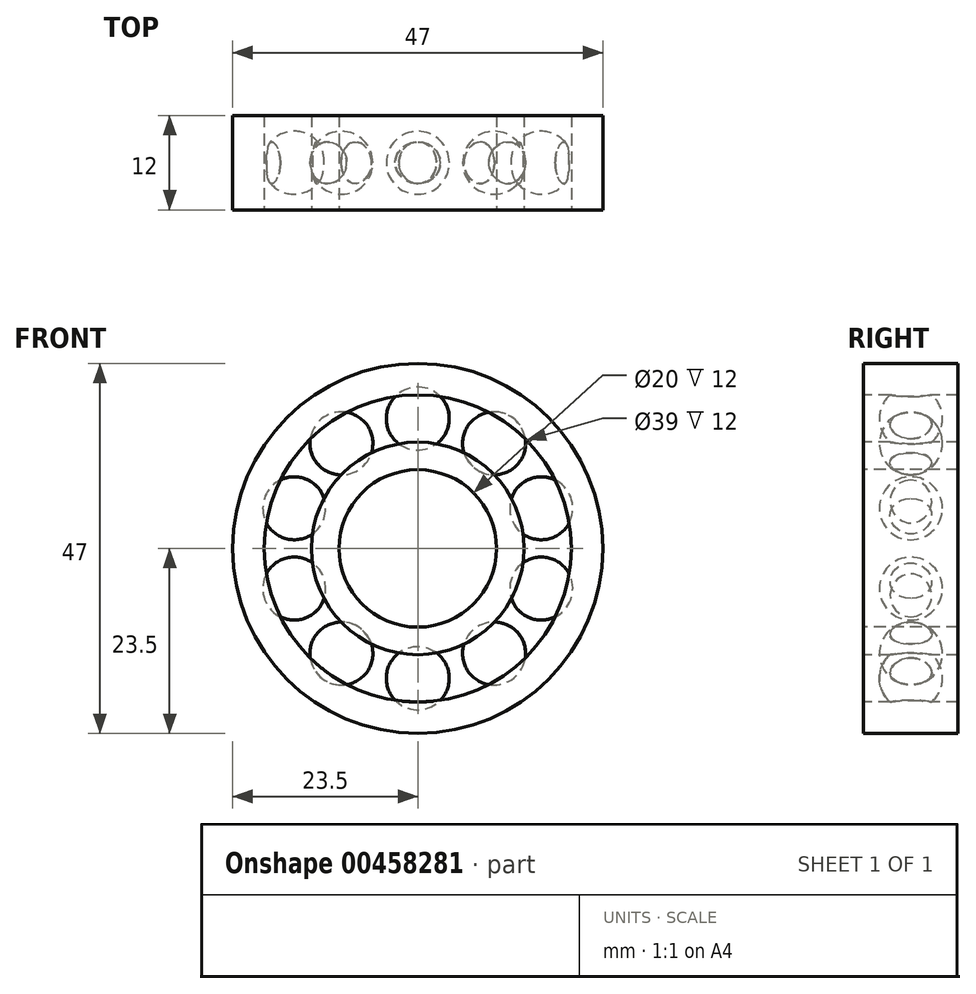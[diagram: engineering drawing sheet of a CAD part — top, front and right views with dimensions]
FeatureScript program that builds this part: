
annotation { "Feature Type Name" : "Feature", "Feature Type Description" : "" }
export const myFeature = defineFeature(function(context is Context, id is Id, definition is map)
    precondition{}
    {
        {
            var Q0;
            Q0=qCreatedBy(makeId("Right.planeOp"),FACE);
            var sketch = newSketch(context, id + "F0", { "sketchPlane" : qUnion([Q0])});
            skLineSegment(sketch, "E0.bottom", {"start": v(-6, 13.5) * mm, "end": v(6, 13.5) * mm});
            skLineSegment(sketch, "E0.top", {"start": v(-6, 10) * mm, "end": v(6, 10) * mm});
            skLineSegment(sketch, "E0.left", {"start": v(-6, 13.5) * mm, "end": v(-6, 10) * mm});
            skLineSegment(sketch, "E0.right", {"start": v(6, 13.5) * mm, "end": v(6, 10) * mm});
            skLineSegment(sketch, "E1.bottom", {"start": v(-6, 23.5) * mm, "end": v(6, 23.5) * mm});
            skLineSegment(sketch, "E1.top", {"start": v(-6, 19.5) * mm, "end": v(6, 19.5) * mm});
            skLineSegment(sketch, "E1.left", {"start": v(-6, 23.5) * mm, "end": v(-6, 19.5) * mm});
            skLineSegment(sketch, "E1.right", {"start": v(6, 23.5) * mm, "end": v(6, 19.5) * mm});
            skLineSegment(sketch, "E2", {"start": v(-39, 0) * mm, "end": v(27.89, 0) * mm, "construction": true});
            skSolve(sketch);
        }
        {
            var Q0;
            Q0 = qSketchRegion(id + "F0", true);
            var Q1;
            Q1=sQuery(id+"F0.wireOp",EDGE,"E2");
            revolve(context, id + "F1", {"entities" : qUnion([Q0]), "axis" : qUnion([Q1]), "revolveType" : RevolveType.FULL});
        }
        {
            var Q0;
            Q0=qCreatedBy(makeId("Front.planeOp"),FACE);
            var sketch = newSketch(context, id + "F2", { "sketchPlane" : qUnion([Q0])});
            skArc(sketch, "E3", {"start": v(0, 12.5) * mm, "mid": v(4, 16.5) * mm, "end": v(0, 20.5) * mm});
            skLineSegment(sketch, "E4", {"start": v(0, 10.56) * mm, "end": v(0, 20.96) * mm, "construction": true});
            skLineSegment(sketch, "E5", {"start": v(0, 20.5) * mm, "end": v(0, 12.5) * mm});
            skPoint(sketch, "E6.center", {"position": v(0, 0) * mm});
            skLineSegment(sketch, "E7", {"start": v(0, 32.3) * mm, "end": v(0, -27.67) * mm, "construction": true});
            skSolve(sketch);
        }
        {
            var Q0;
            Q0 = qSketchRegion(id + "F2", true);
            var Q1;
            Q1=sQuery(id+"F2.wireOp",EDGE,"E4");
            revolve(context, id + "F3", {"entities" : qUnion([Q0]), "axis" : qUnion([Q1]), "revolveType" : RevolveType.FULL});
        }
        {
            var Q0;
            Q0=makeQuery(id+"F3.opRevolve","SWEPT_BODY",BODY,{"disambiguationData":[OSD([sQuery(id+"F2.wireOp",EDGE,"E3"),sQuery(id+"F2.wireOp",EDGE,"E5")])]});
            var Q1;
            Q1=makeQuery(id+"F1.opRevolve","SWEPT_EDGE",EDGE,{"disambiguationData":[OSD([sQuery(id+"F0.wireOp",EDGE,"E0.top"),sQuery(id+"F0.wireOp",EDGE,"E0.left")])]});
            circularPattern(context, id + "F4", {"operationType" : NewBodyOperationType.ADD, "entities" : qUnion([Q0]), "axis" : qUnion([Q1]), "angle" : 360 * degree, "instanceCount" : 10, "equalSpace" : true});
        }
    });
